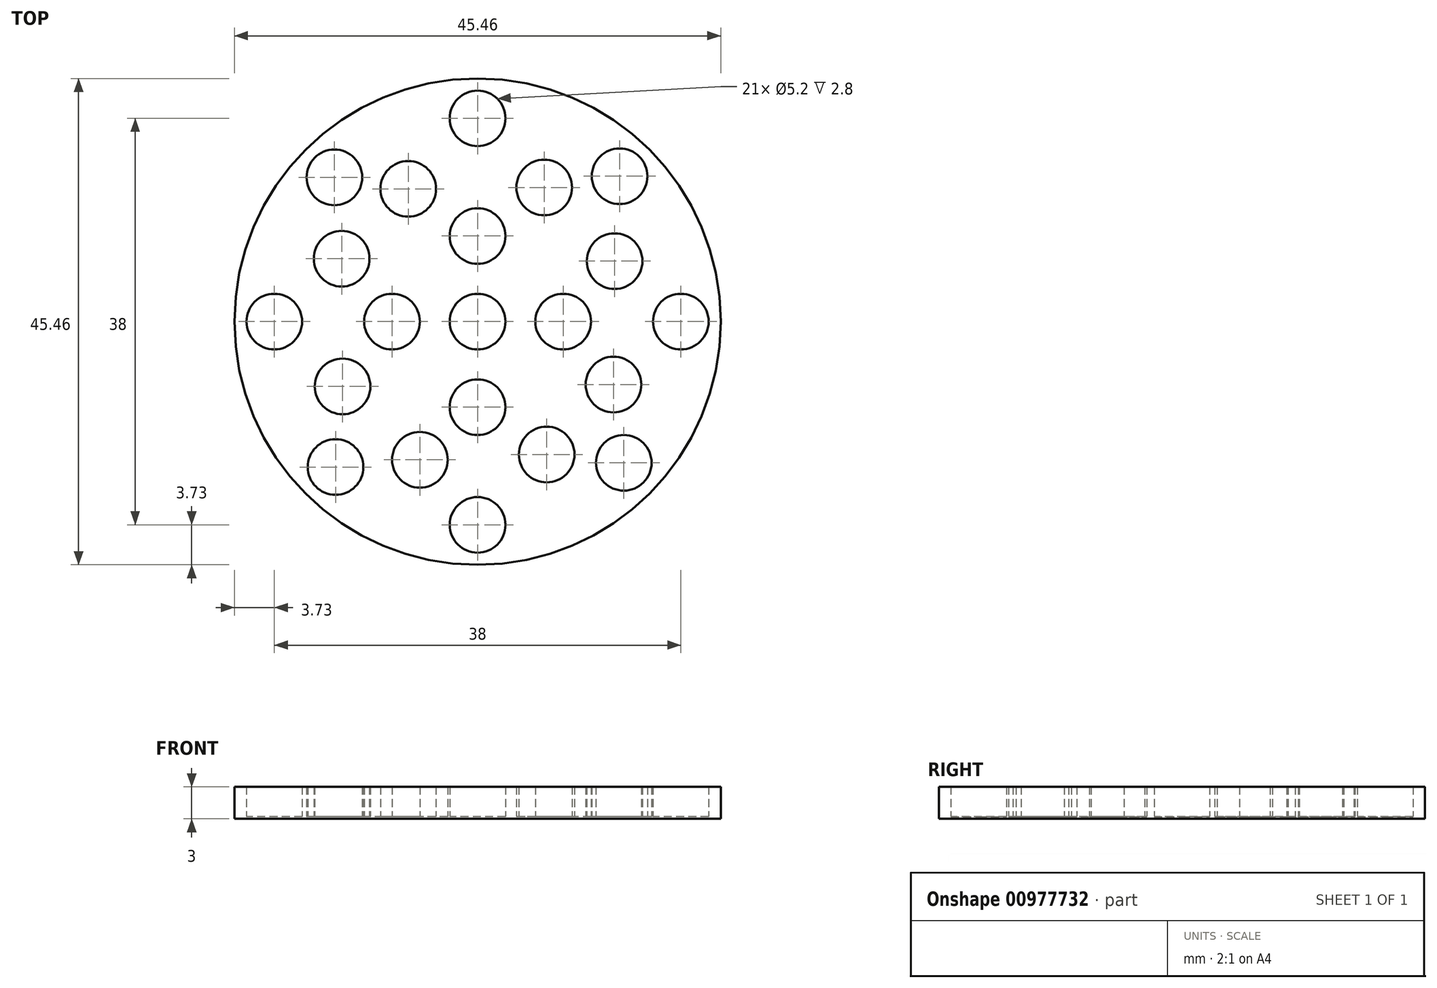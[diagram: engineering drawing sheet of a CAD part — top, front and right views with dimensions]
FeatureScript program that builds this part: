
annotation { "Feature Type Name" : "Feature", "Feature Type Description" : "" }
export const myFeature = defineFeature(function(context is Context, id is Id, definition is map)
    precondition{}
    {
        {
            var Q0;
            Q0=qCreatedBy(makeId("Top.planeOp"),FACE);
            var sketch = newSketch(context, id + "F0", { "sketchPlane" : qUnion([Q0])});
            skCircle(sketch, "E0", {"center": v(0, 0) * mm, "radius": 22.73 * mm});
            skCircle(sketch, "E1", {"center": v(-12.7, 5.88) * mm, "radius": 2.6 * mm});
            skCircle(sketch, "E2", {"center": v(0, 0) * mm, "radius": 8 * mm});
            skCircle(sketch, "E3", {"center": v(0, 0) * mm, "radius": 2.6 * mm});
            skCircle(sketch, "E4", {"center": v(-6.48, 12.4) * mm, "radius": 2.6 * mm});
            skCircle(sketch, "E5", {"center": v(6.23, 12.54) * mm, "radius": 2.6 * mm});
            skCircle(sketch, "E6", {"center": v(12.8, 5.65) * mm, "radius": 2.6 * mm});
            skCircle(sketch, "E7", {"center": v(-12.62, -6.06) * mm, "radius": 2.6 * mm});
            skCircle(sketch, "E8", {"center": v(-5.4, -12.92) * mm, "radius": 2.6 * mm});
            skCircle(sketch, "E9", {"center": v(12.7, -5.88) * mm, "radius": 2.6 * mm});
            skCircle(sketch, "E10", {"center": v(6.46, -12.42) * mm, "radius": 2.6 * mm});
            skCircle(sketch, "E11", {"center": v(0, 8) * mm, "radius": 2.6 * mm});
            skCircle(sketch, "E12", {"center": v(8, 0) * mm, "radius": 2.6 * mm});
            skCircle(sketch, "E13", {"center": v(0, -8) * mm, "radius": 2.6 * mm});
            skCircle(sketch, "E14", {"center": v(-8, 0) * mm, "radius": 2.6 * mm});
            skCircle(sketch, "E15", {"center": v(0, 0) * mm, "radius": 14 * mm});
            skCircle(sketch, "E16", {"center": v(0, 0) * mm, "radius": 19 * mm});
            skCircle(sketch, "E17", {"center": v(-19, 0) * mm, "radius": 2.6 * mm});
            skCircle(sketch, "E18", {"center": v(0, 19) * mm, "radius": 2.6 * mm});
            skCircle(sketch, "E19", {"center": v(0, -19) * mm, "radius": 2.6 * mm});
            skCircle(sketch, "E20", {"center": v(19, 0) * mm, "radius": 2.6 * mm});
            skCircle(sketch, "E21", {"center": v(-13.38, 13.49) * mm, "radius": 2.6 * mm});
            skCircle(sketch, "E22", {"center": v(13.28, 13.59) * mm, "radius": 2.6 * mm});
            skCircle(sketch, "E23", {"center": v(13.67, -13.2) * mm, "radius": 2.6 * mm});
            skCircle(sketch, "E24", {"center": v(-13.28, -13.6) * mm, "radius": 2.6 * mm});
            skSolve(sketch);
        }
        {
            var Q0;
            Q0=makeQuery(id+"F0.imprint","IMPRINT",FACE,{"disambiguationData":[TD([[makeQuery(id+"F0.imprint","IMPRINT",EDGE,{"derivedFrom":sQuery(id+"F0.wireOp",EDGE,"E0")}),1.0]])]});
            var Q1;
            {var subQ14=sQuery(id+"F0.wireOp",EDGE,"E15");var subQ23=sQuery(id+"F0.wireOp",EDGE,"E1");var subQ24=makeQuery(id+"F0.imprint","INTERSECT",VERTEX,{"disambiguationData":[OD(0.0)],"derivedFrom":[subQ23,subQ14]});Q1=makeQuery(id+"F0.imprint","IMPRINT",FACE,{"disambiguationData":[TD([[makeQuery(id+"F0.imprint","IMPRINT",EDGE,{"disambiguationData":[TD([[subQ24,-1.0]])],"derivedFrom":subQ23}),-1.0]])]});}
            var Q2;
            {var subQ0=sQuery(id+"F0.wireOp",EDGE,"E15");var subQ5=sQuery(id+"F0.wireOp",EDGE,"E1");var subQ31=makeQuery(id+"F0.imprint","INTERSECT",VERTEX,{"disambiguationData":[OD(0.0)],"derivedFrom":[subQ5,subQ0]});Q2=makeQuery(id+"F0.imprint","IMPRINT",FACE,{"disambiguationData":[TD([[makeQuery(id+"F0.imprint","IMPRINT",EDGE,{"disambiguationData":[TD([[subQ31,1.0]])],"derivedFrom":subQ5}),-1.0]])]});}
            var Q3;
            Q3=makeQuery(id+"F0.imprint","IMPRINT",FACE,{"disambiguationData":[TD([[makeQuery(id+"F0.imprint","IMPRINT",EDGE,{"derivedFrom":sQuery(id+"F0.wireOp",EDGE,"E3")}),-1.0]])]});
            var Q4;
            {var subQ0=sQuery(id+"F0.wireOp",EDGE,"E24");var subQ1=sQuery(id+"F0.wireOp",EDGE,"E16");var subQ2=makeQuery(id+"F0.imprint","INTERSECT",VERTEX,{"disambiguationData":[OD(0.0)],"derivedFrom":[subQ1,subQ0]});Q4=makeQuery(id+"F0.imprint","IMPRINT",FACE,{"disambiguationData":[TD([[makeQuery(id+"F0.imprint","IMPRINT",EDGE,{"disambiguationData":[TD([[subQ2,-1.0]])],"derivedFrom":subQ1}),1.0]])]});}
            var Q5;
            {var subQ0=sQuery(id+"F0.wireOp",EDGE,"E15");var subQ1=sQuery(id+"F0.wireOp",EDGE,"E7");var subQ2=makeQuery(id+"F0.imprint","INTERSECT",VERTEX,{"disambiguationData":[OD(0.0)],"derivedFrom":[subQ1,subQ0]});Q5=makeQuery(id+"F0.imprint","IMPRINT",FACE,{"disambiguationData":[TD([[makeQuery(id+"F0.imprint","IMPRINT",EDGE,{"disambiguationData":[TD([[subQ2,-1.0]])],"derivedFrom":subQ1}),1.0]])]});}
            var Q6;
            {var subQ0=sQuery(id+"F0.wireOp",EDGE,"E19");var subQ1=sQuery(id+"F0.wireOp",EDGE,"E16");var subQ2=makeQuery(id+"F0.imprint","INTERSECT",VERTEX,{"disambiguationData":[OD(0.0)],"derivedFrom":[subQ1,subQ0]});Q6=makeQuery(id+"F0.imprint","IMPRINT",FACE,{"disambiguationData":[TD([[makeQuery(id+"F0.imprint","IMPRINT",EDGE,{"disambiguationData":[TD([[subQ2,-1.0]])],"derivedFrom":subQ1}),1.0]])]});}
            var Q7;
            {var subQ0=sQuery(id+"F0.wireOp",EDGE,"E19");var subQ1=sQuery(id+"F0.wireOp",EDGE,"E16");var subQ2=makeQuery(id+"F0.imprint","INTERSECT",VERTEX,{"disambiguationData":[OD(0.0)],"derivedFrom":[subQ1,subQ0]});Q7=makeQuery(id+"F0.imprint","IMPRINT",FACE,{"disambiguationData":[TD([[makeQuery(id+"F0.imprint","IMPRINT",EDGE,{"disambiguationData":[TD([[subQ2,-1.0]])],"derivedFrom":subQ1}),-1.0]])]});}
            var Q8;
            {var subQ0=sQuery(id+"F0.wireOp",EDGE,"E11");var subQ1=sQuery(id+"F0.wireOp",EDGE,"E2");var subQ2=makeQuery(id+"F0.imprint","INTERSECT",VERTEX,{"disambiguationData":[OD(0.0)],"derivedFrom":[subQ1,subQ0]});Q8=makeQuery(id+"F0.imprint","IMPRINT",FACE,{"disambiguationData":[TD([[makeQuery(id+"F0.imprint","IMPRINT",EDGE,{"disambiguationData":[TD([[subQ2,-1.0]])],"derivedFrom":subQ1}),-1.0]])]});}
            var Q9;
            {var subQ0=sQuery(id+"F0.wireOp",EDGE,"E21");var subQ1=sQuery(id+"F0.wireOp",EDGE,"E16");var subQ2=makeQuery(id+"F0.imprint","INTERSECT",VERTEX,{"disambiguationData":[OD(0.0)],"derivedFrom":[subQ1,subQ0]});Q9=makeQuery(id+"F0.imprint","IMPRINT",FACE,{"disambiguationData":[TD([[makeQuery(id+"F0.imprint","IMPRINT",EDGE,{"disambiguationData":[TD([[subQ2,-1.0]])],"derivedFrom":subQ1}),1.0]])]});}
            var Q10;
            {var subQ0=sQuery(id+"F0.wireOp",EDGE,"E15");var subQ1=sQuery(id+"F0.wireOp",EDGE,"E6");var subQ2=makeQuery(id+"F0.imprint","INTERSECT",VERTEX,{"disambiguationData":[OD(0.0)],"derivedFrom":[subQ1,subQ0]});Q10=makeQuery(id+"F0.imprint","IMPRINT",FACE,{"disambiguationData":[TD([[makeQuery(id+"F0.imprint","IMPRINT",EDGE,{"disambiguationData":[TD([[subQ2,1.0]])],"derivedFrom":subQ1}),1.0]])]});}
            var Q11;
            {var subQ0=sQuery(id+"F0.wireOp",EDGE,"E14");var subQ1=sQuery(id+"F0.wireOp",EDGE,"E2");var subQ2=makeQuery(id+"F0.imprint","INTERSECT",VERTEX,{"disambiguationData":[OD(0.0)],"derivedFrom":[subQ1,subQ0]});Q11=makeQuery(id+"F0.imprint","IMPRINT",FACE,{"disambiguationData":[TD([[makeQuery(id+"F0.imprint","IMPRINT",EDGE,{"disambiguationData":[TD([[subQ2,-1.0]])],"derivedFrom":subQ1}),-1.0]])]});}
            var Q12;
            {var subQ0=sQuery(id+"F0.wireOp",EDGE,"E13");var subQ1=sQuery(id+"F0.wireOp",EDGE,"E2");var subQ2=makeQuery(id+"F0.imprint","INTERSECT",VERTEX,{"disambiguationData":[OD(0.0)],"derivedFrom":[subQ1,subQ0]});Q12=makeQuery(id+"F0.imprint","IMPRINT",FACE,{"disambiguationData":[TD([[makeQuery(id+"F0.imprint","IMPRINT",EDGE,{"disambiguationData":[TD([[subQ2,-1.0]])],"derivedFrom":subQ1}),1.0]])]});}
            var Q13;
            {var subQ0=sQuery(id+"F0.wireOp",EDGE,"E15");var subQ1=sQuery(id+"F0.wireOp",EDGE,"E4");var subQ2=makeQuery(id+"F0.imprint","INTERSECT",VERTEX,{"disambiguationData":[OD(0.0)],"derivedFrom":[subQ1,subQ0]});Q13=makeQuery(id+"F0.imprint","IMPRINT",FACE,{"disambiguationData":[TD([[makeQuery(id+"F0.imprint","IMPRINT",EDGE,{"disambiguationData":[TD([[subQ2,-1.0]])],"derivedFrom":subQ1}),1.0]])]});}
            var Q14;
            {var subQ0=sQuery(id+"F0.wireOp",EDGE,"E15");var subQ1=sQuery(id+"F0.wireOp",EDGE,"E5");var subQ2=makeQuery(id+"F0.imprint","INTERSECT",VERTEX,{"disambiguationData":[OD(0.0)],"derivedFrom":[subQ1,subQ0]});Q14=makeQuery(id+"F0.imprint","IMPRINT",FACE,{"disambiguationData":[TD([[makeQuery(id+"F0.imprint","IMPRINT",EDGE,{"disambiguationData":[TD([[subQ2,1.0]])],"derivedFrom":subQ1}),1.0]])]});}
            var Q15;
            {var subQ0=sQuery(id+"F0.wireOp",EDGE,"E23");var subQ1=sQuery(id+"F0.wireOp",EDGE,"E16");var subQ2=makeQuery(id+"F0.imprint","INTERSECT",VERTEX,{"disambiguationData":[OD(0.0)],"derivedFrom":[subQ1,subQ0]});Q15=makeQuery(id+"F0.imprint","IMPRINT",FACE,{"disambiguationData":[TD([[makeQuery(id+"F0.imprint","IMPRINT",EDGE,{"disambiguationData":[TD([[subQ2,-1.0]])],"derivedFrom":subQ1}),1.0]])]});}
            var Q16;
            {var subQ0=sQuery(id+"F0.wireOp",EDGE,"E15");var subQ1=sQuery(id+"F0.wireOp",EDGE,"E9");var subQ2=makeQuery(id+"F0.imprint","INTERSECT",VERTEX,{"disambiguationData":[OD(0.0)],"derivedFrom":[subQ1,subQ0]});Q16=makeQuery(id+"F0.imprint","IMPRINT",FACE,{"disambiguationData":[TD([[makeQuery(id+"F0.imprint","IMPRINT",EDGE,{"disambiguationData":[TD([[subQ2,-1.0]])],"derivedFrom":subQ1}),1.0]])]});}
            var Q17;
            {var subQ0=sQuery(id+"F0.wireOp",EDGE,"E18");var subQ1=sQuery(id+"F0.wireOp",EDGE,"E16");var subQ2=makeQuery(id+"F0.imprint","INTERSECT",VERTEX,{"disambiguationData":[OD(0.0)],"derivedFrom":[subQ1,subQ0]});Q17=makeQuery(id+"F0.imprint","IMPRINT",FACE,{"disambiguationData":[TD([[makeQuery(id+"F0.imprint","IMPRINT",EDGE,{"disambiguationData":[TD([[subQ2,-1.0]])],"derivedFrom":subQ1}),-1.0]])]});}
            var Q18;
            {var subQ0=sQuery(id+"F0.wireOp",EDGE,"E22");var subQ1=sQuery(id+"F0.wireOp",EDGE,"E16");var subQ2=makeQuery(id+"F0.imprint","INTERSECT",VERTEX,{"disambiguationData":[OD(0.0)],"derivedFrom":[subQ1,subQ0]});Q18=makeQuery(id+"F0.imprint","IMPRINT",FACE,{"disambiguationData":[TD([[makeQuery(id+"F0.imprint","IMPRINT",EDGE,{"disambiguationData":[TD([[subQ2,-1.0]])],"derivedFrom":subQ1}),1.0]])]});}
            var Q19;
            {var subQ0=sQuery(id+"F0.wireOp",EDGE,"E20");var subQ1=sQuery(id+"F0.wireOp",EDGE,"E16");var subQ2=makeQuery(id+"F0.imprint","INTERSECT",VERTEX,{"disambiguationData":[OD(0.0)],"derivedFrom":[subQ1,subQ0]});Q19=makeQuery(id+"F0.imprint","IMPRINT",FACE,{"disambiguationData":[TD([[makeQuery(id+"F0.imprint","IMPRINT",EDGE,{"disambiguationData":[TD([[subQ2,1.0]])],"derivedFrom":subQ1}),1.0]])]});}
            var Q20;
            {var subQ0=sQuery(id+"F0.wireOp",EDGE,"E20");var subQ1=sQuery(id+"F0.wireOp",EDGE,"E16");var subQ2=makeQuery(id+"F0.imprint","INTERSECT",VERTEX,{"disambiguationData":[OD(0.0)],"derivedFrom":[subQ1,subQ0]});Q20=makeQuery(id+"F0.imprint","IMPRINT",FACE,{"disambiguationData":[TD([[makeQuery(id+"F0.imprint","IMPRINT",EDGE,{"disambiguationData":[TD([[subQ2,1.0]])],"derivedFrom":subQ1}),-1.0]])]});}
            var Q21;
            {var subQ0=sQuery(id+"F0.wireOp",EDGE,"E18");var subQ1=sQuery(id+"F0.wireOp",EDGE,"E16");var subQ2=makeQuery(id+"F0.imprint","INTERSECT",VERTEX,{"disambiguationData":[OD(0.0)],"derivedFrom":[subQ1,subQ0]});Q21=makeQuery(id+"F0.imprint","IMPRINT",FACE,{"disambiguationData":[TD([[makeQuery(id+"F0.imprint","IMPRINT",EDGE,{"disambiguationData":[TD([[subQ2,-1.0]])],"derivedFrom":subQ1}),1.0]])]});}
            var Q22;
            {var subQ0=sQuery(id+"F0.wireOp",EDGE,"E12");var subQ1=sQuery(id+"F0.wireOp",EDGE,"E2");var subQ2=makeQuery(id+"F0.imprint","INTERSECT",VERTEX,{"disambiguationData":[OD(0.0)],"derivedFrom":[subQ1,subQ0]});Q22=makeQuery(id+"F0.imprint","IMPRINT",FACE,{"disambiguationData":[TD([[makeQuery(id+"F0.imprint","IMPRINT",EDGE,{"disambiguationData":[TD([[subQ2,1.0]])],"derivedFrom":subQ1}),1.0]])]});}
            var Q23;
            {var subQ0=sQuery(id+"F0.wireOp",EDGE,"E15");var subQ1=sQuery(id+"F0.wireOp",EDGE,"E6");var subQ2=makeQuery(id+"F0.imprint","INTERSECT",VERTEX,{"disambiguationData":[OD(0.0)],"derivedFrom":[subQ1,subQ0]});Q23=makeQuery(id+"F0.imprint","IMPRINT",FACE,{"disambiguationData":[TD([[makeQuery(id+"F0.imprint","IMPRINT",EDGE,{"disambiguationData":[TD([[subQ2,-1.0]])],"derivedFrom":subQ1}),1.0]])]});}
            var Q24;
            {var subQ0=sQuery(id+"F0.wireOp",EDGE,"E14");var subQ1=sQuery(id+"F0.wireOp",EDGE,"E2");var subQ2=makeQuery(id+"F0.imprint","INTERSECT",VERTEX,{"disambiguationData":[OD(0.0)],"derivedFrom":[subQ1,subQ0]});Q24=makeQuery(id+"F0.imprint","IMPRINT",FACE,{"disambiguationData":[TD([[makeQuery(id+"F0.imprint","IMPRINT",EDGE,{"disambiguationData":[TD([[subQ2,-1.0]])],"derivedFrom":subQ1}),1.0]])]});}
            var Q25;
            {var subQ0=sQuery(id+"F0.wireOp",EDGE,"E15");var subQ1=sQuery(id+"F0.wireOp",EDGE,"E1");var subQ2=makeQuery(id+"F0.imprint","INTERSECT",VERTEX,{"disambiguationData":[OD(0.0)],"derivedFrom":[subQ1,subQ0]});Q25=makeQuery(id+"F0.imprint","IMPRINT",FACE,{"disambiguationData":[TD([[makeQuery(id+"F0.imprint","IMPRINT",EDGE,{"disambiguationData":[TD([[subQ2,1.0]])],"derivedFrom":subQ1}),1.0]])]});}
            var Q26;
            {var subQ0=sQuery(id+"F0.wireOp",EDGE,"E17");var subQ1=sQuery(id+"F0.wireOp",EDGE,"E16");var subQ2=makeQuery(id+"F0.imprint","INTERSECT",VERTEX,{"disambiguationData":[OD(0.0)],"derivedFrom":[subQ1,subQ0]});Q26=makeQuery(id+"F0.imprint","IMPRINT",FACE,{"disambiguationData":[TD([[makeQuery(id+"F0.imprint","IMPRINT",EDGE,{"disambiguationData":[TD([[subQ2,-1.0]])],"derivedFrom":subQ1}),-1.0]])]});}
            var Q27;
            {var subQ0=sQuery(id+"F0.wireOp",EDGE,"E22");var subQ1=sQuery(id+"F0.wireOp",EDGE,"E16");var subQ2=makeQuery(id+"F0.imprint","INTERSECT",VERTEX,{"disambiguationData":[OD(0.0)],"derivedFrom":[subQ1,subQ0]});Q27=makeQuery(id+"F0.imprint","IMPRINT",FACE,{"disambiguationData":[TD([[makeQuery(id+"F0.imprint","IMPRINT",EDGE,{"disambiguationData":[TD([[subQ2,-1.0]])],"derivedFrom":subQ1}),-1.0]])]});}
            var Q28;
            {var subQ0=sQuery(id+"F0.wireOp",EDGE,"E13");var subQ1=sQuery(id+"F0.wireOp",EDGE,"E2");var subQ2=makeQuery(id+"F0.imprint","INTERSECT",VERTEX,{"disambiguationData":[OD(0.0)],"derivedFrom":[subQ1,subQ0]});Q28=makeQuery(id+"F0.imprint","IMPRINT",FACE,{"disambiguationData":[TD([[makeQuery(id+"F0.imprint","IMPRINT",EDGE,{"disambiguationData":[TD([[subQ2,-1.0]])],"derivedFrom":subQ1}),-1.0]])]});}
            var Q29;
            {var subQ0=sQuery(id+"F0.wireOp",EDGE,"E15");var subQ1=sQuery(id+"F0.wireOp",EDGE,"E5");var subQ2=makeQuery(id+"F0.imprint","INTERSECT",VERTEX,{"disambiguationData":[OD(0.0)],"derivedFrom":[subQ1,subQ0]});Q29=makeQuery(id+"F0.imprint","IMPRINT",FACE,{"disambiguationData":[TD([[makeQuery(id+"F0.imprint","IMPRINT",EDGE,{"disambiguationData":[TD([[subQ2,-1.0]])],"derivedFrom":subQ1}),1.0]])]});}
            var Q30;
            {var subQ0=sQuery(id+"F0.wireOp",EDGE,"E15");var subQ1=sQuery(id+"F0.wireOp",EDGE,"E1");var subQ2=makeQuery(id+"F0.imprint","INTERSECT",VERTEX,{"disambiguationData":[OD(0.0)],"derivedFrom":[subQ1,subQ0]});Q30=makeQuery(id+"F0.imprint","IMPRINT",FACE,{"disambiguationData":[TD([[makeQuery(id+"F0.imprint","IMPRINT",EDGE,{"disambiguationData":[TD([[subQ2,-1.0]])],"derivedFrom":subQ1}),1.0]])]});}
            var Q31;
            {var subQ0=sQuery(id+"F0.wireOp",EDGE,"E15");var subQ1=sQuery(id+"F0.wireOp",EDGE,"E8");var subQ2=makeQuery(id+"F0.imprint","INTERSECT",VERTEX,{"disambiguationData":[OD(0.0)],"derivedFrom":[subQ1,subQ0]});Q31=makeQuery(id+"F0.imprint","IMPRINT",FACE,{"disambiguationData":[TD([[makeQuery(id+"F0.imprint","IMPRINT",EDGE,{"disambiguationData":[TD([[subQ2,-1.0]])],"derivedFrom":subQ1}),1.0]])]});}
            var Q32;
            {var subQ0=sQuery(id+"F0.wireOp",EDGE,"E15");var subQ1=sQuery(id+"F0.wireOp",EDGE,"E10");var subQ2=makeQuery(id+"F0.imprint","INTERSECT",VERTEX,{"disambiguationData":[OD(0.0)],"derivedFrom":[subQ1,subQ0]});Q32=makeQuery(id+"F0.imprint","IMPRINT",FACE,{"disambiguationData":[TD([[makeQuery(id+"F0.imprint","IMPRINT",EDGE,{"disambiguationData":[TD([[subQ2,1.0]])],"derivedFrom":subQ1}),1.0]])]});}
            var Q33;
            {var subQ0=sQuery(id+"F0.wireOp",EDGE,"E21");var subQ1=sQuery(id+"F0.wireOp",EDGE,"E16");var subQ2=makeQuery(id+"F0.imprint","INTERSECT",VERTEX,{"disambiguationData":[OD(0.0)],"derivedFrom":[subQ1,subQ0]});Q33=makeQuery(id+"F0.imprint","IMPRINT",FACE,{"disambiguationData":[TD([[makeQuery(id+"F0.imprint","IMPRINT",EDGE,{"disambiguationData":[TD([[subQ2,-1.0]])],"derivedFrom":subQ1}),-1.0]])]});}
            var Q34;
            {var subQ0=sQuery(id+"F0.wireOp",EDGE,"E17");var subQ1=sQuery(id+"F0.wireOp",EDGE,"E16");var subQ2=makeQuery(id+"F0.imprint","INTERSECT",VERTEX,{"disambiguationData":[OD(0.0)],"derivedFrom":[subQ1,subQ0]});Q34=makeQuery(id+"F0.imprint","IMPRINT",FACE,{"disambiguationData":[TD([[makeQuery(id+"F0.imprint","IMPRINT",EDGE,{"disambiguationData":[TD([[subQ2,-1.0]])],"derivedFrom":subQ1}),1.0]])]});}
            var Q35;
            {var subQ0=sQuery(id+"F0.wireOp",EDGE,"E15");var subQ1=sQuery(id+"F0.wireOp",EDGE,"E7");var subQ2=makeQuery(id+"F0.imprint","INTERSECT",VERTEX,{"disambiguationData":[OD(0.0)],"derivedFrom":[subQ1,subQ0]});Q35=makeQuery(id+"F0.imprint","IMPRINT",FACE,{"disambiguationData":[TD([[makeQuery(id+"F0.imprint","IMPRINT",EDGE,{"disambiguationData":[TD([[subQ2,1.0]])],"derivedFrom":subQ1}),1.0]])]});}
            var Q36;
            {var subQ0=sQuery(id+"F0.wireOp",EDGE,"E15");var subQ1=sQuery(id+"F0.wireOp",EDGE,"E9");var subQ2=makeQuery(id+"F0.imprint","INTERSECT",VERTEX,{"disambiguationData":[OD(0.0)],"derivedFrom":[subQ1,subQ0]});Q36=makeQuery(id+"F0.imprint","IMPRINT",FACE,{"disambiguationData":[TD([[makeQuery(id+"F0.imprint","IMPRINT",EDGE,{"disambiguationData":[TD([[subQ2,1.0]])],"derivedFrom":subQ1}),1.0]])]});}
            var Q37;
            {var subQ0=sQuery(id+"F0.wireOp",EDGE,"E15");var subQ1=sQuery(id+"F0.wireOp",EDGE,"E4");var subQ2=makeQuery(id+"F0.imprint","INTERSECT",VERTEX,{"disambiguationData":[OD(0.0)],"derivedFrom":[subQ1,subQ0]});Q37=makeQuery(id+"F0.imprint","IMPRINT",FACE,{"disambiguationData":[TD([[makeQuery(id+"F0.imprint","IMPRINT",EDGE,{"disambiguationData":[TD([[subQ2,1.0]])],"derivedFrom":subQ1}),1.0]])]});}
            var Q38;
            {var subQ0=sQuery(id+"F0.wireOp",EDGE,"E11");var subQ1=sQuery(id+"F0.wireOp",EDGE,"E2");var subQ2=makeQuery(id+"F0.imprint","INTERSECT",VERTEX,{"disambiguationData":[OD(0.0)],"derivedFrom":[subQ1,subQ0]});Q38=makeQuery(id+"F0.imprint","IMPRINT",FACE,{"disambiguationData":[TD([[makeQuery(id+"F0.imprint","IMPRINT",EDGE,{"disambiguationData":[TD([[subQ2,-1.0]])],"derivedFrom":subQ1}),1.0]])]});}
            var Q39;
            {var subQ0=sQuery(id+"F0.wireOp",EDGE,"E23");var subQ1=sQuery(id+"F0.wireOp",EDGE,"E16");var subQ2=makeQuery(id+"F0.imprint","INTERSECT",VERTEX,{"disambiguationData":[OD(0.0)],"derivedFrom":[subQ1,subQ0]});Q39=makeQuery(id+"F0.imprint","IMPRINT",FACE,{"disambiguationData":[TD([[makeQuery(id+"F0.imprint","IMPRINT",EDGE,{"disambiguationData":[TD([[subQ2,-1.0]])],"derivedFrom":subQ1}),-1.0]])]});}
            var Q40;
            {var subQ0=sQuery(id+"F0.wireOp",EDGE,"E24");var subQ1=sQuery(id+"F0.wireOp",EDGE,"E16");var subQ2=makeQuery(id+"F0.imprint","INTERSECT",VERTEX,{"disambiguationData":[OD(0.0)],"derivedFrom":[subQ1,subQ0]});Q40=makeQuery(id+"F0.imprint","IMPRINT",FACE,{"disambiguationData":[TD([[makeQuery(id+"F0.imprint","IMPRINT",EDGE,{"disambiguationData":[TD([[subQ2,-1.0]])],"derivedFrom":subQ1}),-1.0]])]});}
            var Q41;
            {var subQ0=sQuery(id+"F0.wireOp",EDGE,"E12");var subQ1=sQuery(id+"F0.wireOp",EDGE,"E2");var subQ2=makeQuery(id+"F0.imprint","INTERSECT",VERTEX,{"disambiguationData":[OD(0.0)],"derivedFrom":[subQ1,subQ0]});Q41=makeQuery(id+"F0.imprint","IMPRINT",FACE,{"disambiguationData":[TD([[makeQuery(id+"F0.imprint","IMPRINT",EDGE,{"disambiguationData":[TD([[subQ2,1.0]])],"derivedFrom":subQ1}),-1.0]])]});}
            var Q42;
            {var subQ0=sQuery(id+"F0.wireOp",EDGE,"E15");var subQ1=sQuery(id+"F0.wireOp",EDGE,"E8");var subQ2=makeQuery(id+"F0.imprint","INTERSECT",VERTEX,{"disambiguationData":[OD(0.0)],"derivedFrom":[subQ1,subQ0]});Q42=makeQuery(id+"F0.imprint","IMPRINT",FACE,{"disambiguationData":[TD([[makeQuery(id+"F0.imprint","IMPRINT",EDGE,{"disambiguationData":[TD([[subQ2,1.0]])],"derivedFrom":subQ1}),1.0]])]});}
            var Q43;
            {var subQ0=sQuery(id+"F0.wireOp",EDGE,"E15");var subQ1=sQuery(id+"F0.wireOp",EDGE,"E10");var subQ2=makeQuery(id+"F0.imprint","INTERSECT",VERTEX,{"disambiguationData":[OD(0.0)],"derivedFrom":[subQ1,subQ0]});Q43=makeQuery(id+"F0.imprint","IMPRINT",FACE,{"disambiguationData":[TD([[makeQuery(id+"F0.imprint","IMPRINT",EDGE,{"disambiguationData":[TD([[subQ2,-1.0]])],"derivedFrom":subQ1}),1.0]])]});}
            var Q44;
            Q44=makeQuery(id+"F0.imprint","IMPRINT",FACE,{"disambiguationData":[TD([[makeQuery(id+"F0.imprint","IMPRINT",EDGE,{"derivedFrom":sQuery(id+"F0.wireOp",EDGE,"E3")}),1.0]])]});
            extrude(context, id + "F1", {"entities" : qUnion([Q0, Q1, Q2, Q3, Q4, Q5, Q6, Q7, Q8, Q9, Q10, Q11, Q12, Q13, Q14, Q15, Q16, Q17, Q18, Q19, Q20, Q21, Q22, Q23, Q24, Q25, Q26, Q27, Q28, Q29, Q30, Q31, Q32, Q33, Q34, Q35, Q36, Q37, Q38, Q39, Q40, Q41, Q42, Q43, Q44]), "depth" : 0.2 * mm, "offsetDistance" : 25 * mm});
        }
        {
            var Q0;
            Q0=makeQuery(id+"F0.imprint","IMPRINT",FACE,{"disambiguationData":[TD([[makeQuery(id+"F0.imprint","IMPRINT",EDGE,{"derivedFrom":sQuery(id+"F0.wireOp",EDGE,"E3")}),-1.0]])]});
            var Q1;
            {var subQ0=sQuery(id+"F0.wireOp",EDGE,"E15");var subQ5=sQuery(id+"F0.wireOp",EDGE,"E1");var subQ31=makeQuery(id+"F0.imprint","INTERSECT",VERTEX,{"disambiguationData":[OD(0.0)],"derivedFrom":[subQ5,subQ0]});Q1=makeQuery(id+"F0.imprint","IMPRINT",FACE,{"disambiguationData":[TD([[makeQuery(id+"F0.imprint","IMPRINT",EDGE,{"disambiguationData":[TD([[subQ31,1.0]])],"derivedFrom":subQ5}),-1.0]])]});}
            var Q2;
            {var subQ14=sQuery(id+"F0.wireOp",EDGE,"E15");var subQ23=sQuery(id+"F0.wireOp",EDGE,"E1");var subQ24=makeQuery(id+"F0.imprint","INTERSECT",VERTEX,{"disambiguationData":[OD(0.0)],"derivedFrom":[subQ23,subQ14]});Q2=makeQuery(id+"F0.imprint","IMPRINT",FACE,{"disambiguationData":[TD([[makeQuery(id+"F0.imprint","IMPRINT",EDGE,{"disambiguationData":[TD([[subQ24,-1.0]])],"derivedFrom":subQ23}),-1.0]])]});}
            var Q3;
            Q3=makeQuery(id+"F0.imprint","IMPRINT",FACE,{"disambiguationData":[TD([[makeQuery(id+"F0.imprint","IMPRINT",EDGE,{"derivedFrom":sQuery(id+"F0.wireOp",EDGE,"E0")}),1.0]])]});
            extrude(context, id + "F2", {"entities" : qUnion([Q0, Q1, Q2, Q3]), "operationType" : NewBodyOperationType.ADD, "depth" : 3 * mm, "offsetDistance" : 25 * mm});
        }
    });
